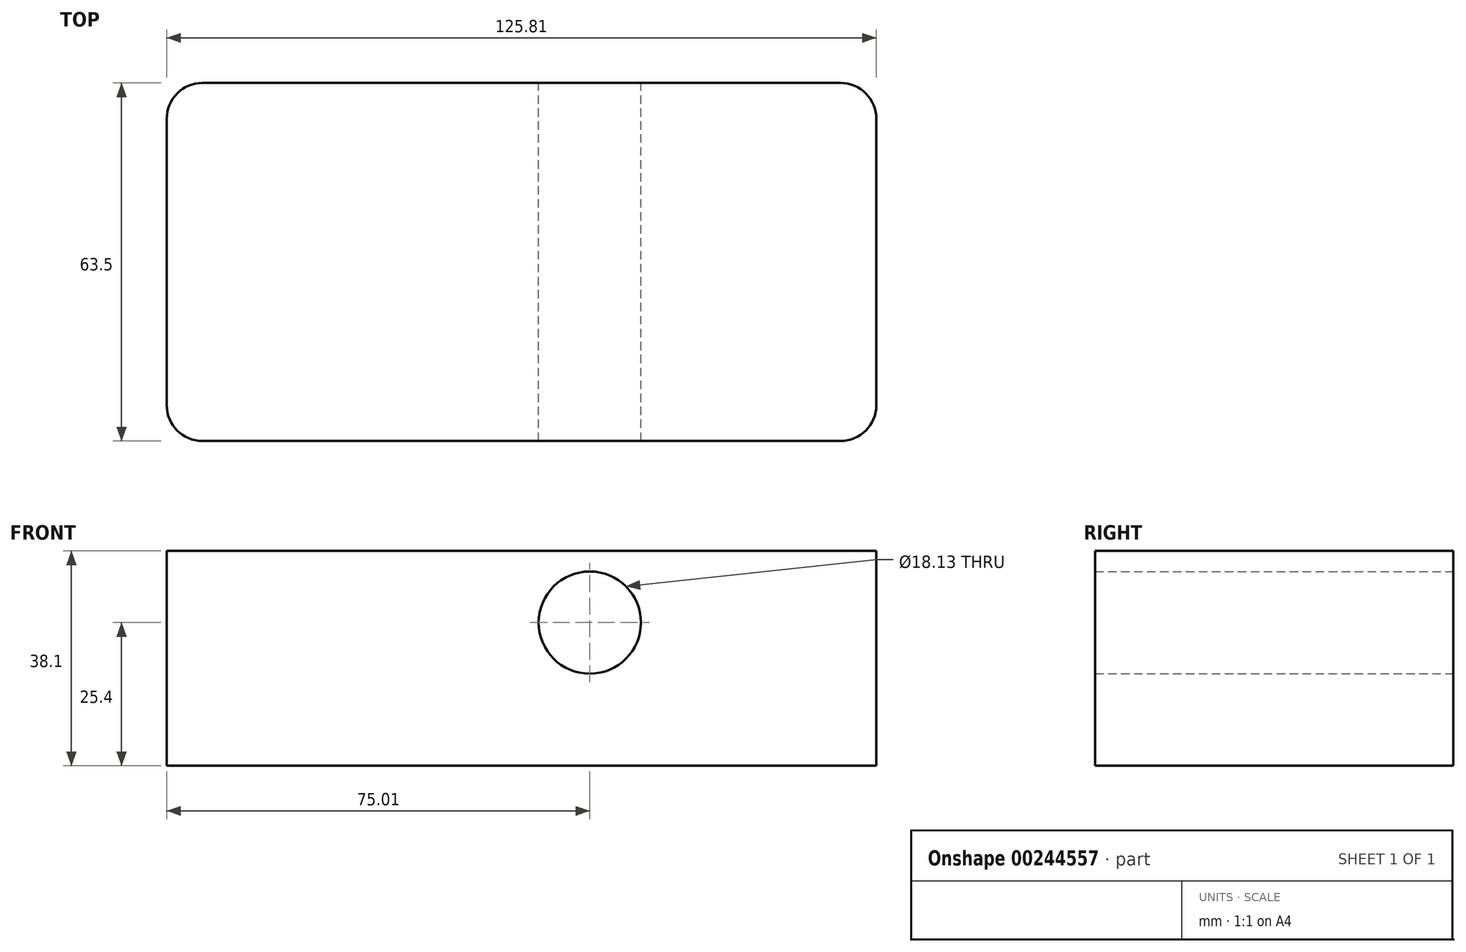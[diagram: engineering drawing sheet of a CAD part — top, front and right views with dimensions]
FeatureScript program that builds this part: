
annotation { "Feature Type Name" : "Feature", "Feature Type Description" : "" }
export const myFeature = defineFeature(function(context is Context, id is Id, definition is map)
    precondition{}
    {
        {
            var Q0;
            Q0=qCreatedBy(makeId("Top.planeOp"),FACE);
            var sketch = newSketch(context, id + "F0", { "sketchPlane" : qUnion([Q0])});
            skLineSegment(sketch, "E0", {"start": v(-6.35, 0) * mm, "end": v(-119.46, 0) * mm});
            skLineSegment(sketch, "E1", {"start": v(-125.8, 57.15) * mm, "end": v(-125.8, 6.35) * mm});
            skLineSegment(sketch, "E2", {"start": v(-119.46, 63.5) * mm, "end": v(-6.35, 63.5) * mm});
            skLineSegment(sketch, "E3", {"start": v(0, 57.15) * mm, "end": v(0, 6.35) * mm});
            skLineSegment(sketch, "E4", {"start": v(-19.2, -101.33) * mm, "end": v(23.43, -108) * mm});
            skLineSegment(sketch, "E5", {"start": v(23.43, -108) * mm, "end": v(12, -106.22) * mm});
            skLineSegment(sketch, "E6", {"start": v(13.22, -108.45) * mm, "end": v(12, -106.22) * mm});
            skPoint(sketch, "E7.visualSharp", {"position": v(0, 63.5) * mm});
            skArc(sketch, "E7.filletArc", {"start": v(0, 57.15) * mm, "mid": v(-1.86, 61.64) * mm, "end": v(-6.35, 63.5) * mm});
            skPoint(sketch, "E8.visualSharp", {"position": v(-125.8, 0) * mm});
            skArc(sketch, "E8.filletArc", {"start": v(-125.8, 6.35) * mm, "mid": v(-123.95, 1.86) * mm, "end": v(-119.46, 0) * mm});
            skPoint(sketch, "E9.visualSharp", {"position": v(-125.8, 63.5) * mm});
            skArc(sketch, "E9.filletArc", {"start": v(-119.46, 63.5) * mm, "mid": v(-123.95, 61.64) * mm, "end": v(-125.8, 57.15) * mm});
            skPoint(sketch, "E10.visualSharp", {"position": v(0, 0) * mm});
            skArc(sketch, "E10.filletArc", {"start": v(-6.35, 0) * mm, "mid": v(-1.86, 1.86) * mm, "end": v(0, 6.35) * mm});
            skSolve(sketch);
        }
        {
            var Q0;
            Q0 = qSketchRegion(id + "F0", true);
            extrude(context, id + "F1", {"entities" : qUnion([Q0]), "depth" : 38.1 * mm});
        }
        {
            var Q0;
            Q0=makeQuery(id+"F1.opExtrude","SWEPT_FACE",FACE,{"disambiguationData":[OSD([sQuery(id+"F0.wireOp",EDGE,"E2")])]});
            var sketch = newSketch(context, id + "F2", { "sketchPlane" : qUnion([Q0])});
            skCircle(sketch, "E11", {"center": v(50.8, 25.4) * mm, "radius": 9.07 * mm});
            skSolve(sketch);
        }
        {
            var Q0;
            Q0 = qSketchRegion(id + "F2", true);
            extrude(context, id + "F3", {"entities" : qUnion([Q0]), "operationType" : NewBodyOperationType.REMOVE, "endBound" : BoundingType.THROUGH_ALL, "oppositeDirection" : true, "depth" : 25.4 * mm});
        }
    });
